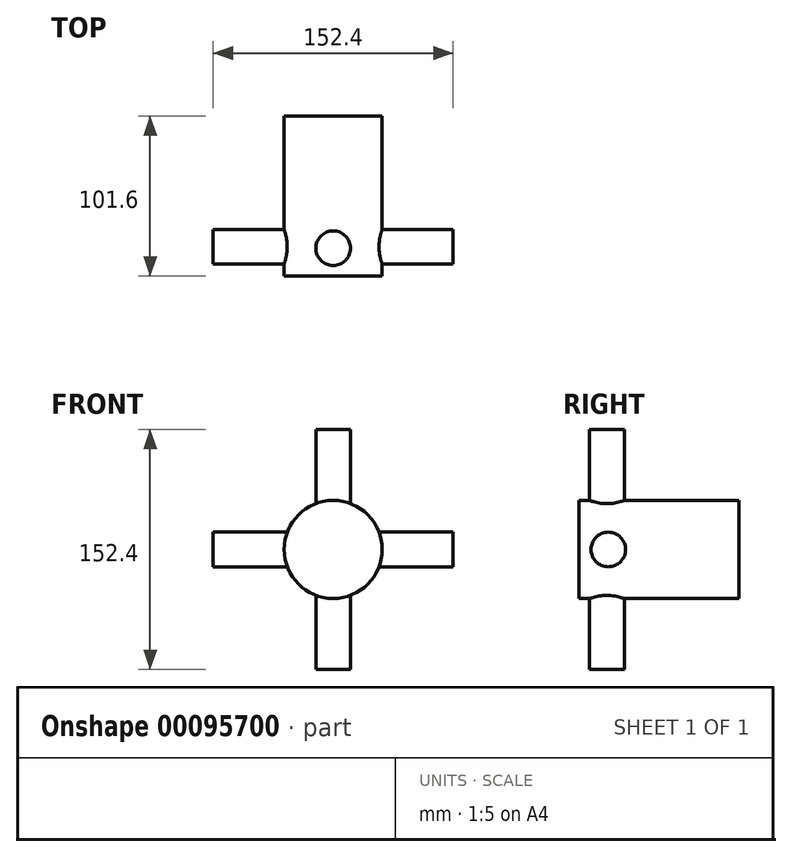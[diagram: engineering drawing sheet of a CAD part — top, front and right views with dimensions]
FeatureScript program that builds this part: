
annotation { "Feature Type Name" : "Feature", "Feature Type Description" : "" }
export const myFeature = defineFeature(function(context is Context, id is Id, definition is map)
    precondition{}
    {
        {
            var Q0;
            Q0=qCreatedBy(makeId("Front.planeOp"),FACE);
            var sketch = newSketch(context, id + "F0", { "sketchPlane" : qUnion([Q0])});
            skCircle(sketch, "E0", {"center": v(0, 0) * mm, "radius": 31.15 * mm});
            skSolve(sketch);
        }
        {
            var Q0;
            Q0 = qSketchRegion(id + "F0", true);
            extrude(context, id + "F1", {"entities" : qUnion([Q0]), "endBound" : BoundingType.SYMMETRIC, "depth" : 101.6 * mm});
        }
        {
            var Q0;
            Q0=qCreatedBy(makeId("Right.planeOp"),FACE);
            var sketch = newSketch(context, id + "F2", { "sketchPlane" : qUnion([Q0])});
            skCircle(sketch, "E1", {"center": v(-32.22, 0) * mm, "radius": 11 * mm});
            skSolve(sketch);
        }
        {
            var Q0;
            Q0=qCreatedBy(makeId("Top.planeOp"),FACE);
            var sketch = newSketch(context, id + "F3", { "sketchPlane" : qUnion([Q0])});
            skCircle(sketch, "E2", {"center": v(0, -33.12) * mm, "radius": 11 * mm});
            skSolve(sketch);
        }
        {
            var Q0;
            Q0 = qSketchRegion(id + "F2", true);
            extrude(context, id + "F4", {"entities" : qUnion([Q0]), "operationType" : NewBodyOperationType.ADD, "endBound" : BoundingType.SYMMETRIC, "depth" : 152.4 * mm});
        }
        {
            var Q0;
            Q0 = qSketchRegion(id + "F3", true);
            extrude(context, id + "F5", {"entities" : qUnion([Q0]), "operationType" : NewBodyOperationType.ADD, "endBound" : BoundingType.SYMMETRIC, "depth" : 152.4 * mm});
        }
    });
